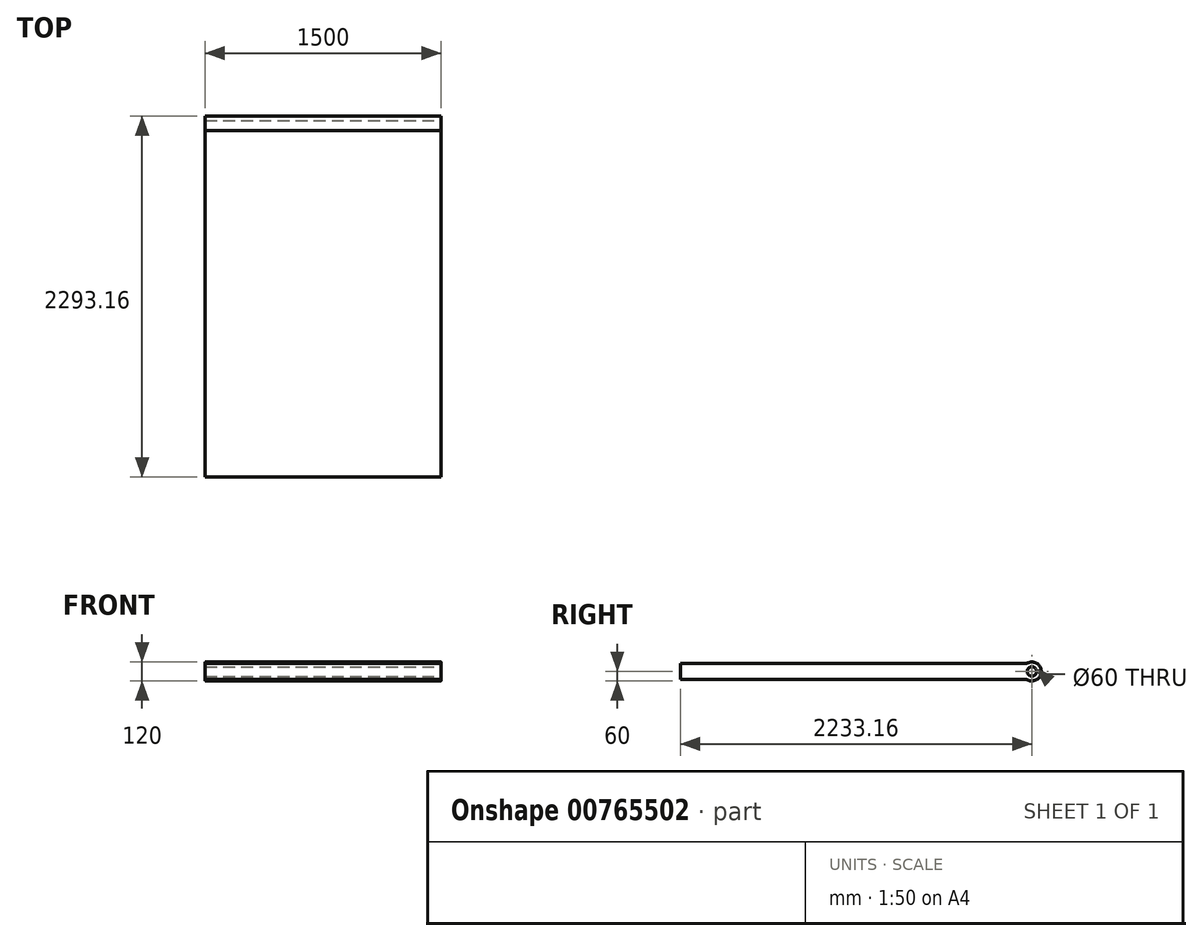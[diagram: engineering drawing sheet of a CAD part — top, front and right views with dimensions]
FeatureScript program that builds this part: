
annotation { "Feature Type Name" : "Feature", "Feature Type Description" : "" }
export const myFeature = defineFeature(function(context is Context, id is Id, definition is map)
    precondition{}
    {
        {
            var Q0;
            Q0=qCreatedBy(makeId("Top.planeOp"),FACE);
            var sketch = newSketch(context, id + "F0", { "sketchPlane" : qUnion([Q0])});
            skLineSegment(sketch, "E0.bottom", {"start": v(-1658.12, 1093.39) * mm, "end": v(-158.12, 1093.39) * mm});
            skLineSegment(sketch, "E0.top", {"start": v(-1658.12, -1106.61) * mm, "end": v(-158.12, -1106.61) * mm});
            skLineSegment(sketch, "E0.left", {"start": v(-1658.12, 1093.39) * mm, "end": v(-1658.12, -1106.61) * mm});
            skLineSegment(sketch, "E0.right", {"start": v(-158.12, 1093.39) * mm, "end": v(-158.12, -1106.61) * mm});
            skSolve(sketch);
        }
        {
            var Q0;
            Q0=makeQuery(id+"F0.imprint","IMPRINT",FACE,{"disambiguationData":[TD([[makeQuery(id+"F0.imprint","IMPRINT",EDGE,{"derivedFrom":sQuery(id+"F0.wireOp",EDGE,"E0.bottom")}),-1.0]])]});
            extrude(context, id + "F1", {"entities" : qUnion([Q0]), "depth" : 100 * mm, "offsetDistance" : 25 * mm});
        }
        {
            var Q0;
            Q0=makeQuery(id+"F1.opExtrude","SWEPT_FACE",FACE,{"disambiguationData":[OSD([sQuery(id+"F0.wireOp",EDGE,"E0.right")])]});
            var sketch = newSketch(context, id + "F2", { "sketchPlane" : qUnion([Q0])});
            skCircle(sketch, "E1", {"center": v(1126.55, 50) * mm, "radius": 60 * mm});
            skPoint(sketch, "E2", {"position": v(1093.39, 50) * mm});
            skCircle(sketch, "E3", {"center": v(1126.55, 50) * mm, "radius": 30 * mm});
            skSolve(sketch);
        }
        {
            var Q0;
            Q0=makeQuery(id+"F2.imprint","IMPRINT",FACE,{"disambiguationData":[TD([[makeQuery(id+"F2.imprint","IMPRINT",EDGE,{"derivedFrom":sQuery(id+"F2.wireOp",EDGE,"E3")}),-1.0]])]});
            var Q1;
            Q1=makeQuery(id+"F1.opExtrude","SWEPT_FACE",FACE,{"disambiguationData":[OSD([sQuery(id+"F0.wireOp",EDGE,"E0.left")])]});
            extrude(context, id + "F3", {"entities" : qUnion([Q0]), "operationType" : NewBodyOperationType.ADD, "endBound" : BoundingType.UP_TO_SURFACE, "oppositeDirection" : true, "depth" : 25 * mm, "endBoundEntityFace" : qUnion([Q1]), "offsetDistance" : 25 * mm});
        }
    });
